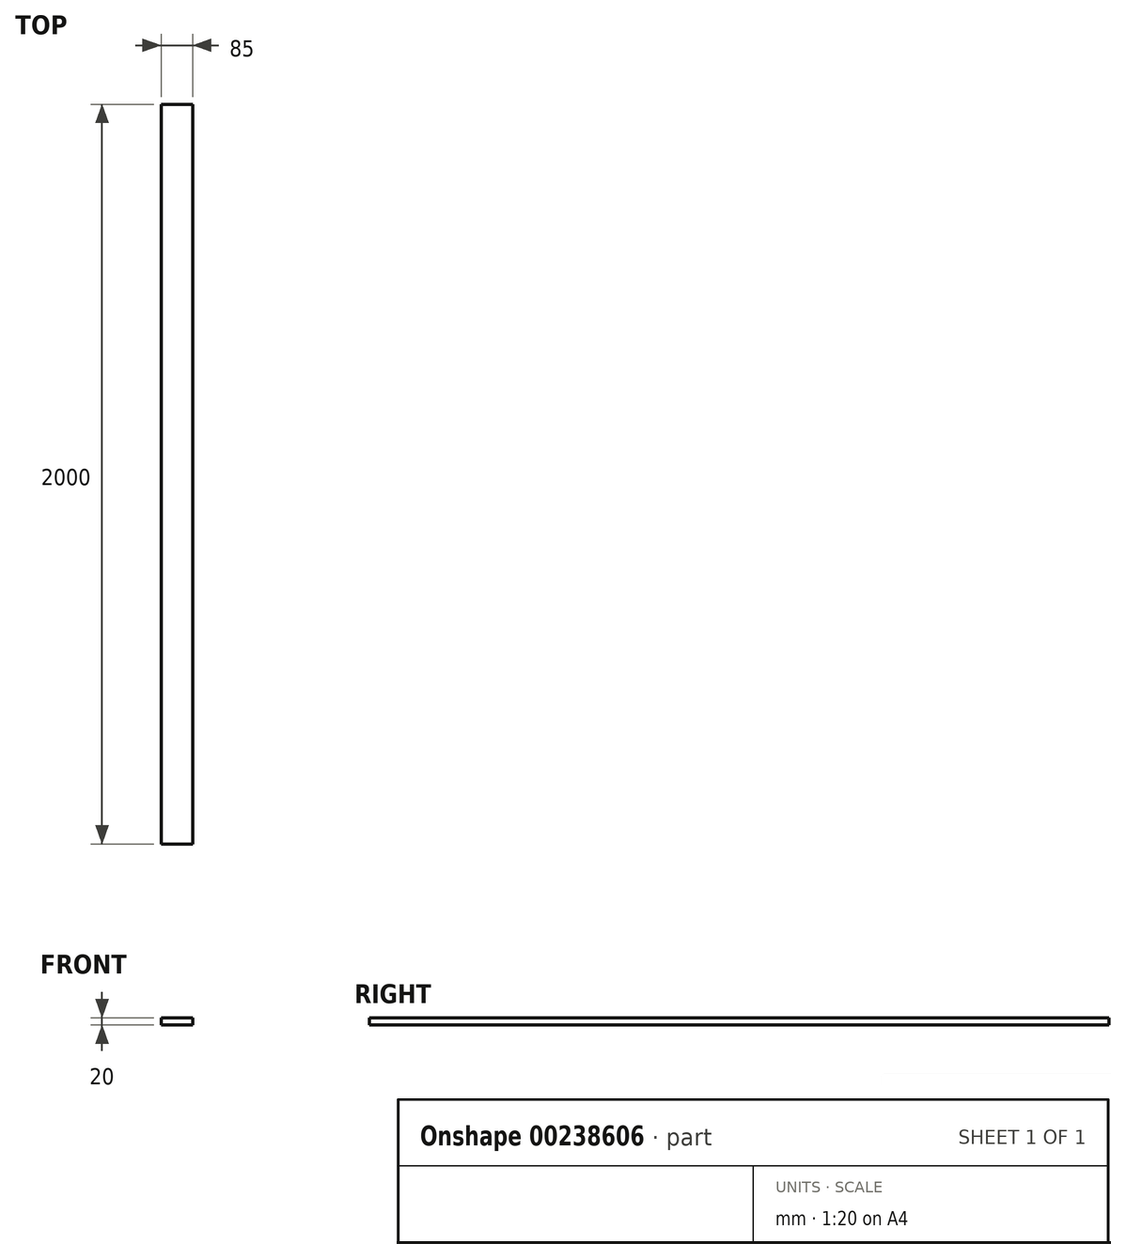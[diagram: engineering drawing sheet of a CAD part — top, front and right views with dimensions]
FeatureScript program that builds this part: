
annotation { "Feature Type Name" : "Feature", "Feature Type Description" : "" }
export const myFeature = defineFeature(function(context is Context, id is Id, definition is map)
    precondition{}
    {
        {
            var Q0;
            Q0=qCreatedBy(makeId("Front.planeOp"),FACE);
            var sketch = newSketch(context, id + "F0", { "sketchPlane" : qUnion([Q0])});
            skLineSegment(sketch, "E0.bottom", {"start": v(42.5, -10) * mm, "end": v(-42.5, -10) * mm});
            skLineSegment(sketch, "E0.top", {"start": v(42.5, 10) * mm, "end": v(-42.5, 10) * mm});
            skLineSegment(sketch, "E0.left", {"start": v(42.5, -10) * mm, "end": v(42.5, 10) * mm});
            skLineSegment(sketch, "E0.right", {"start": v(-42.5, -10) * mm, "end": v(-42.5, 10) * mm});
            skPoint(sketch, "E0.middle", {"position": v(0, 0) * mm});
            skSolve(sketch);
        }
        {
            var Q0;
            Q0=makeQuery(id+"F0.imprint","IMPRINT",FACE,{"disambiguationData":[TD([[makeQuery(id+"F0.imprint","IMPRINT",EDGE,{"derivedFrom":sQuery(id+"F0.wireOp",EDGE,"E0.bottom")}),-1.0]])]});
            extrude(context, id + "F1", {"entities" : qUnion([Q0]), "depth" : 2000 * mm});
        }
    });
